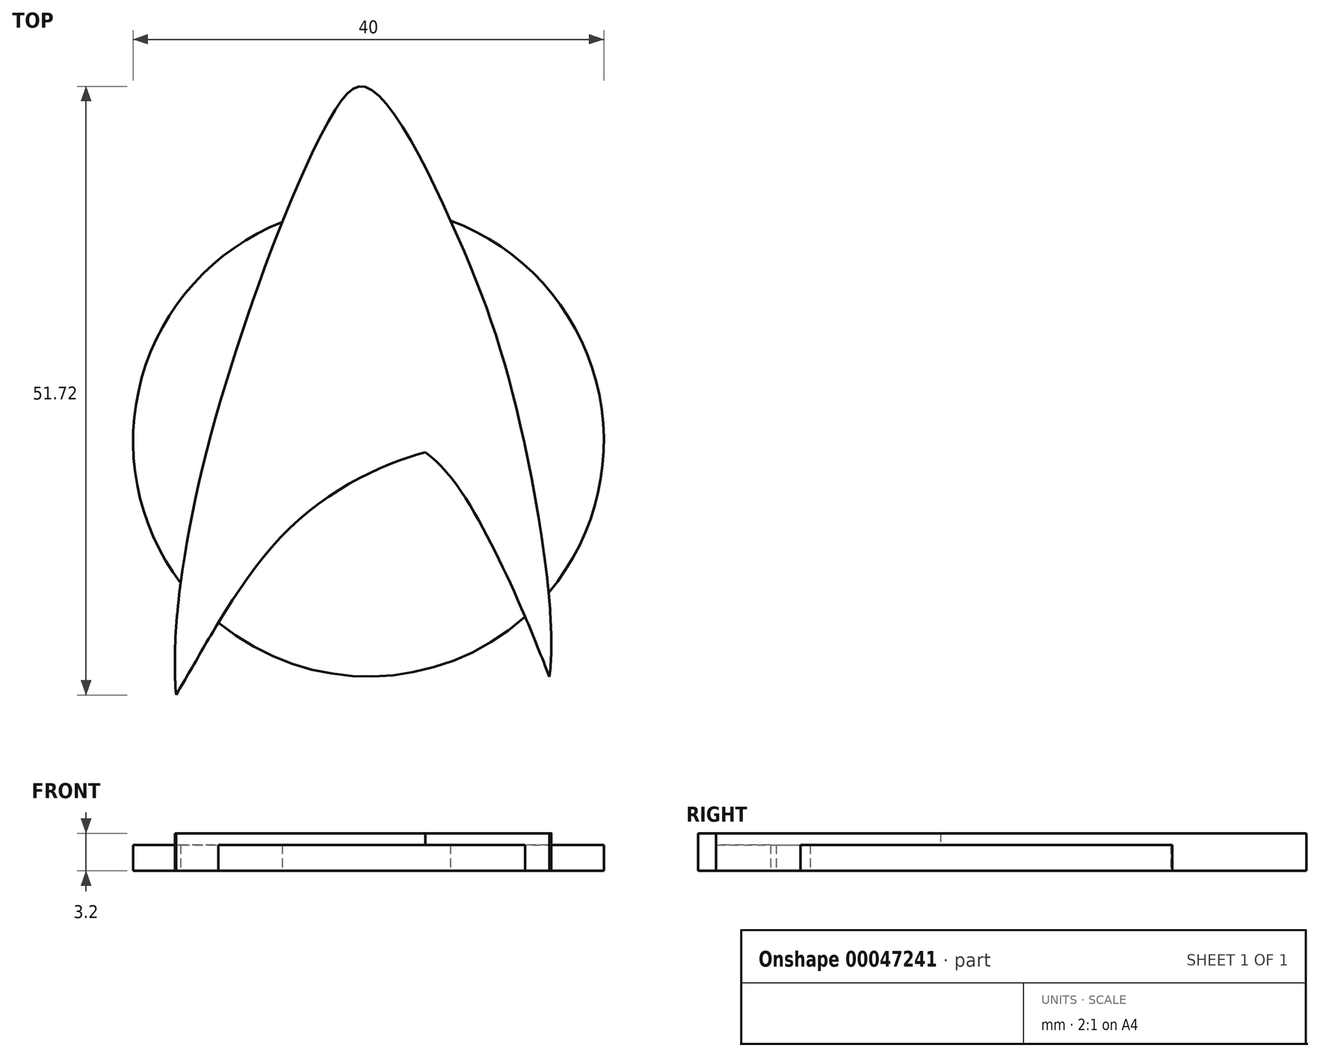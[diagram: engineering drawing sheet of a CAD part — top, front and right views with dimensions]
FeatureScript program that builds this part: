
annotation { "Feature Type Name" : "Feature", "Feature Type Description" : "" }
export const myFeature = defineFeature(function(context is Context, id is Id, definition is map)
    precondition{}
    {
        {
            var Q0;
            Q0=qCreatedBy(makeId("Top.planeOp"),FACE);
            var sketch = newSketch(context, id + "F0", { "sketchPlane" : qUnion([Q0])});
            skLineSegment(sketch, "E0", {"start": v(0, 0) * mm, "end": v(63.5, 0) * mm, "construction": true});
            skLineSegment(sketch, "E1", {"start": v(63.5, 0) * mm, "end": v(63.5, 63.5) * mm, "construction": true});
            skLineSegment(sketch, "E2", {"start": v(63.5, 63.5) * mm, "end": v(0, 63.5) * mm, "construction": true});
            skLineSegment(sketch, "E3", {"start": v(0, 63.5) * mm, "end": v(0, 0) * mm, "construction": true});
            skLineSegment(sketch, "E4", {"start": v(0, 63.5) * mm, "end": v(63.5, 0) * mm, "construction": true});
            skCircle(sketch, "E5", {"center": v(31.75, 31.75) * mm, "radius": 20 * mm});
            skFitSpline(sketch, "E6", {"points": [v(15.4, 10.18) * mm, v(25.33, 24.62) * mm, v(36.58, 30.79) * mm], "startDerivative": vector(15.48, 26.03) * mm, "endDerivative": vector(20.18, 5) * mm});
            skFitSpline(sketch, "E7", {"points": [v(47.14, 11.71) * mm, v(42.08, 23.2) * mm, v(36.58, 30.79) * mm], "startDerivative": vector(-9.45, 24.34) * mm, "endDerivative": vector(-14, 9.74) * mm});
            skLineSegment(sketch, "E8", {"start": v(31.75, 31.75) * mm, "end": v(31.75, 61.75) * mm, "construction": true});
            skFitSpline(sketch, "E9", {"points": [v(15.4, 10.18) * mm, v(18.05, 31.1) * mm, v(28.75, 59.63) * mm, v(31.75, 61.75) * mm, v(39.41, 48.94) * mm, v(44.6, 33.35) * mm, v(47.14, 11.71) * mm], "startDerivative": vector(-6.86, 77) * mm, "endDerivative": vector(-10.44, -81.3) * mm});
            skSolve(sketch);
        }
        {
            var Q0;
            Q0 = qSketchRegion(id + "F0", true);
            extrude(context, id + "F1", {"entities" : qUnion([Q0]), "depth" : 2.2 * mm});
        }
        {
            var Q0;
            {var subQ0=sQuery(id+"F0.wireOp",EDGE,"E9");var subQ1=sQuery(id+"F0.wireOp",EDGE,"E5");var subQ2=makeQuery(id+"F0.imprint","INTERSECT",VERTEX,{"disambiguationData":[OD(0.0)],"derivedFrom":[subQ1,subQ0]});Q0=makeQuery(id+"F0.imprint","IMPRINT",FACE,{"disambiguationData":[TD([[makeQuery(id+"F0.imprint","IMPRINT",EDGE,{"disambiguationData":[TD([[subQ2,1.0]])],"derivedFrom":subQ1}),-1.0]])]});}
            var Q1;
            {var subQ0=sQuery(id+"F0.wireOp",EDGE,"E7");var subQ1=sQuery(id+"F0.wireOp",EDGE,"E5");var subQ2=makeQuery(id+"F0.imprint","INTERSECT",VERTEX,{"derivedFrom":[subQ1,subQ0]});Q1=makeQuery(id+"F0.imprint","IMPRINT",FACE,{"disambiguationData":[TD([[makeQuery(id+"F0.imprint","IMPRINT",EDGE,{"disambiguationData":[TD([[subQ2,-1.0]])],"derivedFrom":subQ1}),-1.0]])]});}
            var Q2;
            {var subQ0=sQuery(id+"F0.wireOp",EDGE,"E9");var subQ1=sQuery(id+"F0.wireOp",EDGE,"E5");var subQ2=makeQuery(id+"F0.imprint","INTERSECT",VERTEX,{"disambiguationData":[OD(2.0)],"derivedFrom":[subQ1,subQ0]});Q2=makeQuery(id+"F0.imprint","IMPRINT",FACE,{"disambiguationData":[TD([[makeQuery(id+"F0.imprint","IMPRINT",EDGE,{"disambiguationData":[TD([[subQ2,-1.0]])],"derivedFrom":subQ1}),-1.0]])]});}
            var Q3;
            {var subQ1=sQuery(id+"F0.wireOp",EDGE,"E5");var subQ3=sQuery(id+"F0.wireOp",EDGE,"E9");var subQ10=makeQuery(id+"F0.imprint","INTERSECT",VERTEX,{"disambiguationData":[OD(0.0)],"derivedFrom":[subQ1,subQ3]});Q3=makeQuery(id+"F0.imprint","IMPRINT",FACE,{"disambiguationData":[TD([[makeQuery(id+"F0.imprint","IMPRINT",EDGE,{"disambiguationData":[TD([[subQ10,1.0]])],"derivedFrom":subQ1}),1.0]])]});}
            extrude(context, id + "F2", {"entities" : qUnion([Q0, Q1, Q2, Q3]), "operationType" : NewBodyOperationType.ADD, "depth" : 3.2 * mm});
        }
    });
